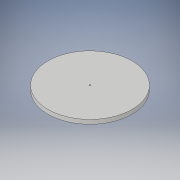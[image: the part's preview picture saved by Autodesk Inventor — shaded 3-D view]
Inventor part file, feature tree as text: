
AUTODESK INVENTOR PART (.ipt)
format: ipt  version: 2017 (Build 210142000, 142)  size: 114,176 bytes
history: native  units: mm
features: sketch x3, extrude x2, hole x1, projected_geometry x1
ambient origin geometry x8: Origin, YZ Plane, XZ Plane, XY Plane, X Axis, Y Axis, Z Axis, Center Point
bodies: Solid1 (feature_tree)
feature tree (7):
  extrude  "Extrusion1"  Depth=3.0mm
  extrude  "Extrusion2"  Depth=15.0mm
  hole  "Hole1"  [1 undecoded]
  sketch  "Sketch1"  dims[d0=60.0mm d1=3.0mm]
  sketch  "Sketch2"  dims[d2=0.0mm d3=15.0mm]
  projected_geometry  "Projected Loop1"
  sketch  "Sketch3"  dims[d5=3.0mm d6=3.0mm d7=3.0mm d8=0.0mm d9=1.0mm d10=6.0mm d11=4.0mm d12=2.0mm d13=90.0deg d14=8.0mm d15=20.594885mm]
note: 1 required parameter value undecoded (feature->parameter linkage not recoverable at this tier; creation-order binding heuristic only, values carry confidence <= 0.55)
